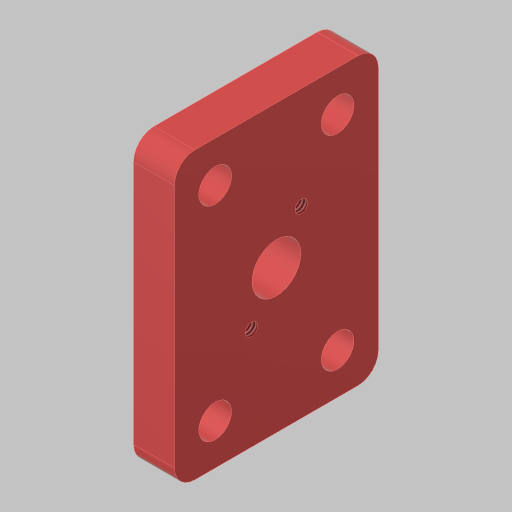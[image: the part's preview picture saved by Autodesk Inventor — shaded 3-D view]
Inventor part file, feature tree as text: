
AUTODESK INVENTOR PART (.ipt)
format: ipt  version: 2023.5 (Build 275446000, 446)  size: 140,800 bytes
history: native  units: in
note: dims shown in document units (in); Inventor stores cm internally (conversion verified against a paired STEP export)
features: sketch x3, extrude x2, hole x2, fillet x1
ambient origin geometry x8: Origin, YZ Plane, XZ Plane, XY Plane, X Axis, Y Axis, Z Axis, Center Point
bodies: Solid1 (feature_tree)
feature tree (8):
  sketch  "Sketch1"  dims[d0=1.75in d1=1.25in]
  extrude  "Extrusion1"  Depth=1.25in
  hole  "Hole1"  [1 undecoded]
  hole  "Hole2"  [1 undecoded]
  extrude  "Extrusion2"  Depth=0.25in
  fillet  "Fillet1"  Radius=0.25in
  sketch  "Sketch2"  dims[d2=1.25in d3=0.75in]
  sketch  "Sketch3"  dims[d4=0.25in d5=0.0in d6=0.201in d7=0.38in d8=0.385in d9=0.25in d10=0.5635in d11=1.0in d12=0.8108in d13=0.586in d14=0.0764in d15=0.198in d16=0.375in d17=0.25in d18=0.5635in d19=1.0in d20=0.8108in d21=0.3in d22=0.25in d23=0.0in d24=0.125in d27=0.25in]
note: 2 required parameter values undecoded (feature->parameter linkage not recoverable at this tier; creation-order binding heuristic only, values carry confidence <= 0.55)
